# Revit family: Hand_Shower-American_Standard-Serin_Shower_Kit-2064.724
name_source: partatom
category: Plumbing Fixtures
revit_build: Autodesk Revit 2015 (Build: 20140606_1530(x64)
units: mm (PartAtom-declared; Revit-internal decimal feet)

## types (3) — shared parameters
Assembly Code = D2010710
CW Connection = Yes
CWFU = 3
Cold Water Connection Diameter = 1/2"
Cold Water Connection Radius = 1/4"
Default Elevation = 44"
Description = Serin Complete Hand Shower Kit
Flow Rate = 2.5 GPM (9.5 L/min)
HW Connection = Yes
HWFU = 3
Height = 24 3/8"
Hot Water Connection Diameter = 1"
Hot Water Connection Radius = 1/4"
Installation Type = Wall-Mounted
Manufacturer = American Standard
Price = Prices may vary. Please consult Manufacturer Representative for most up-to-date price list.
Product Documentation Link = https://www.americanstandard-us.com
Product Page URL = https://www.americanstandard-us.com
URL = https://www.americanstandard-us.com
Vent Connection = No
WFU = 4
Warranty Information = Limited 1-Year Warranty
Waste Connection = No
Width = 3 3/4"

## per-type parameters (varying)
| type | Finish | Material |
| 2064.724.002 | Brass-American Standard-002-Polished Chrome | Brass-American Standard-002-Polished Chrome |
| 2064.724.295 | Brass-American Standard-295-Brushed Nickel | Brass-American Standard-295-Brushed Nickel |
| 2064.724.075 | Brass-American Standard-075-Stainless Steel | Brass-American Standard-075-Stainless Steel |

note: column(s) folded — value = type name in every type: Model

## geometry (parser evidence)
native form markers: Sweep x2
no freeform markers — native parametric forms only
